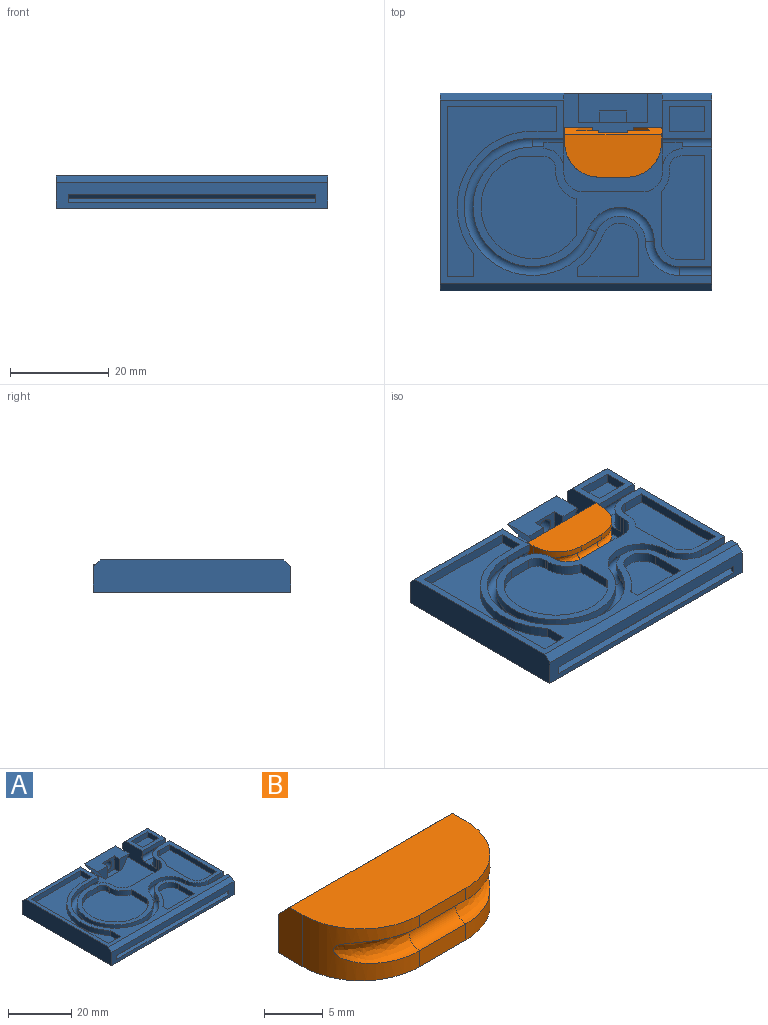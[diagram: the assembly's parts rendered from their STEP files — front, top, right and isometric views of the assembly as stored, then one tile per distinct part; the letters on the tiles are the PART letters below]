
ASSEMBLY  parts=2 mates=1
PART A: 103 faces, bbox 55x40x6.5 mm
  f0: plane 48.34x24.2mm, normal (0,0,1), area 268.4mm2, adj f6,f7,f13,f16,f17,f23,f26,f29
  f1: plane 10x7.7mm, normal (0,0,1), area 41.7mm2, adj f7,f14,f17,f52,f82,f83,f84,f85
  f2: plane 55x37.2mm, normal (0,0,1), area 312mm2, adj f6,f17,f18,f20,f21,f24,f27,f30
  f3: plane 55x5.1mm, normal (0,1,0), area 150.8mm2, adj f6,f7,f8,f9,f17,f18,f19,f34
  f4: plane 14x2.7mm, normal (0,1,0), area 27mm2, adj f8,f9,f10,f43,f56,f57
  f5: plane 55x5.1mm, normal (0,-1,0), area 200.5mm2, adj f17,f18,f19,f54,f64,f65,f66,f67
  f6: plane 16x5.6mm, normal (1,0,0), area 64.8mm2, adj f0,f2,f3,f12,f20,f34,f37,f38
  f7: plane 16x5.6mm, normal (-1,0,0), area 64.8mm2, adj f0,f1,f3,f14,f15,f34,f41,f42
  f8: plane 6x4.6mm, normal (0.82,0,-0.57), area 32.9mm2, adj f3,f4,f11,f34,f43,f55,f56
  f9: plane 6x4.6mm, normal (-0.82,0,-0.57), area 32.9mm2, adj f3,f4,f34,f43,f44,f55,f57
  f10: cylinder r=1.7mm len=3.6mm, axis (0,-1,0), area 36.5mm2, adj f4,f48,f55,f56,f57
  f11: plane 4.6x4.25mm, normal (0,-1,0), area 12.1mm2, adj f8,f34,f43,f46
  f12: cylinder r=1.25mm len=6.24mm, axis (-1,0,0), area 24.8mm2, adj f6,f13,f20,f22,f35,f36,f37
  f13: plane 2.24x1.6mm, normal (0,1,0), area 3.6mm2, adj f0,f12,f23,f36
  f14: plane 10x1.6mm, normal (0,-1,0), area 16mm2, adj f1,f7,f15,f17
  f15: cylinder r=1.25mm len=10mm, axis (-1,0,0), area 46.8mm2, adj f7,f14,f16,f17,f39,f40,f41
  f16: plane 6x1.6mm, normal (0,1,0), area 9.6mm2, adj f0,f15,f17,f40
  f17: plane 40x6.5mm, normal (1,0,0), area 243.4mm2, adj f0,f1,f2,f3,f5,f14,f15,f16
  f18: plane 40x6.5mm, normal (-1,0,0), area 258mm2, adj f2,f3,f5,f19,f53,f54
  f19: plane 55x40mm, normal (0,0,-1), area 2200mm2, adj f3,f5,f17,f18
  f20: plane 6.24x1.6mm, normal (0,-1,0), area 10mm2, adj f2,f6,f12,f21
  f21: cylinder r=13.9mm len=27.8mm, axis (0,0,1), area 96.4mm2, adj f2,f20,f22,f24
  f22: torus R=13mm, axis (0,0,1), area 329.4mm2, adj f12,f21,f23,f25
  f23: cylinder r=12.1mm len=24.2mm, axis (0,0,1), area 83.9mm2, adj f0,f13,f22,f26
  f24: cylinder r=5.1mm len=9.84mm, axis (0,0,-1), area 22.6mm2, adj f2,f21,f25,f27
  f25: torus R=6mm, axis (0,0,-1), area 96.9mm2, adj f22,f24,f26,f28
  f26: cylinder r=6.9mm len=13.31mm, axis (0,0,-1), area 30.5mm2, adj f0,f23,f25,f29
  f27: cylinder r=6.9mm len=6.9mm, axis (0,0,1), area 17.3mm2, adj f2,f24,f28,f30
  f28: torus R=6mm, axis (0,0,1), area 55.1mm2, adj f25,f27,f29,f31
  f29: cylinder r=5.1mm len=5.1mm, axis (0,0,1), area 12.8mm2, adj f0,f26,f28,f32
  f30: plane 6.58x1.6mm, normal (0,1,0), area 10.5mm2, adj f2,f17,f27,f31
  f31: cylinder r=1.25mm len=6.58mm, axis (1,0,0), area 38.4mm2, adj f17,f28,f30,f32
  f32: plane 6.58x1.6mm, normal (0,-1,0), area 10.5mm2, adj f0,f17,f29,f31
  f33: plane 12x5.6mm, normal (0,1,0), area 67.2mm2, adj f0,f34,f50,f51
  f34: plane 20x20mm, normal (0,0,1), area 347.8mm2, adj f3,f6,f7,f8,f9,f11,f33,f44
  f35: plane 1.25x1.25mm, normal (1,0,0), area 0.3mm2, adj f12,f37,f38
  f36: plane 2.47x0.35mm, normal (1,0,0), area 0.7mm2, adj f0,f12,f13,f38
  f37: plane 5.25x4mm, normal (0,0,1), area 8.4mm2, adj f6,f12,f35,f38
  f38: cylinder r=4mm len=4mm, axis (0,0,1), area 23.4mm2, adj f0,f6,f35,f36,f37
  f39: plane 1.25x1.25mm, normal (-1,0,0), area 0.3mm2, adj f15,f41,f42
  f40: plane 2.47x0.35mm, normal (-1,0,0), area 0.7mm2, adj f0,f15,f16,f42
  f41: plane 5.25x4mm, normal (0,0,1), area 8.4mm2, adj f7,f15,f39,f42
  f42: cylinder r=4mm len=4mm, axis (0,0,1), area 23.4mm2, adj f0,f7,f39,f40,f41
  f43: plane 14x6mm, normal (0,0,1), area 70.8mm2, adj f4,f8,f9,f11,f44,f46,f47,f48
  f44: plane 4.6x4.25mm, normal (0,-1,0), area 12.1mm2, adj f9,f34,f43,f47
  f45: plane 5.5x0.5mm, normal (0,1,0), area 2.8mm2, adj f34,f46,f47,f49
  f46: plane 5.1x2.4mm, normal (-1,0,0), area 12.2mm2, adj f11,f43,f45,f48,f49
  f47: plane 5.1x2.4mm, normal (1,0,0), area 12.2mm2, adj f43,f44,f45,f48,f49
  f48: plane 5.5x5.1mm, normal (0,-1,0), area 19mm2, adj f10,f43,f46,f47,f49
  f49: plane 5.5x2.4mm, normal (0,0,1), area 13.2mm2, adj f45,f46,f47,f48
  f50: cylinder r=4mm len=5.6mm, axis (0,0,-1), area 35.2mm2, adj f0,f6,f33,f34
  f51: cylinder r=4mm len=5.6mm, axis (0,0,1), area 35.2mm2, adj f0,f7,f33,f34
  f52: plane 10x1.4mm, normal (0,0.71,0.71), area 19.8mm2, adj f1,f3,f7,f17
  f53: plane 25x1.4mm, normal (0,0.71,0.71), area 49.5mm2, adj f2,f3,f6,f18
  f54: plane 55x1.4mm, normal (0,-0.71,0.71), area 108.9mm2, adj f2,f5,f17,f18
  f55: plane 9.1x0.8mm, normal (0,0.71,0.71), area 8.3mm2, adj f3,f8,f9,f10,f56,f57
  f56: plane 3.86x0.8mm, normal (0,0.71,-0.71), area 3.8mm2, adj f4,f8,f10,f55
  f57: plane 3.86x0.8mm, normal (0,0.71,-0.71), area 3.8mm2, adj f4,f9,f10,f55
  f58: plane 7.5x0.8mm, normal (0,0.71,0.71), area 8.5mm2, adj f3,f7,f59,f60
  f59: plane 7.5x0.8mm, normal (0,0.71,-0.71), area 8.5mm2, adj f3,f7,f58,f60
  f60: plane 1.6x0.8mm, normal (-1,0,0), area 0.6mm2, adj f3,f58,f59
  f61: plane 22.5x0.8mm, normal (0,0.71,-0.71), area 25.5mm2, adj f3,f6,f62,f63
  f62: plane 22.5x0.8mm, normal (0,0.71,0.71), area 25.5mm2, adj f3,f6,f61,f63
  f63: plane 1.6x0.8mm, normal (1,0,0), area 0.6mm2, adj f3,f61,f62
  f64: plane 50x0.8mm, normal (0,-0.71,0.71), area 56.6mm2, adj f5,f65,f66,f67
  f65: plane 50x0.8mm, normal (0,-0.71,-0.71), area 56.6mm2, adj f5,f64,f66,f67
  f66: plane 1.6x0.8mm, normal (-1,0,0), area 0.6mm2, adj f5,f64,f65
  f67: plane 1.6x0.8mm, normal (1,0,0), area 0.6mm2, adj f5,f64,f65
  f68: plane 22.2x2mm, normal (0,-1,0), area 44.4mm2, adj f2,f69,f74,f75
  f69: plane 34.4x2mm, normal (1,0,0), area 68.8mm2, adj f2,f68,f70,f75
  f70: plane 5.46x2mm, normal (-0.01,1,0), area 10.9mm2, adj f2,f69,f71,f75
  f71: plane 4.55x2mm, normal (-1,0,0), area 9.1mm2, adj f2,f70,f72,f75
  f72: cylinder r=15.3mm len=24.92mm, axis (0,0,1), area 68.9mm2, adj f2,f71,f73,f75
  f73: plane 4.84x2mm, normal (0,1,0), area 9.7mm2, adj f2,f72,f74,f75
  f74: plane 4.9x2mm, normal (-1,0,0), area 9.8mm2, adj f2,f68,f73,f75
  f75: plane 34.4x22.2mm, normal (0,0,1), area 245.7mm2, adj f68,f69,f70,f71,f72,f73,f74
  f76: plane 2x1.9mm, normal (1,0,0), area 3.8mm2, adj f2,f77,f80,f81
  f77: plane 12.26x2mm, normal (0,1,0), area 24.5mm2, adj f2,f76,f78,f81
  f78: plane 7.2x2mm, normal (-1,0,0), area 14.4mm2, adj f2,f77,f79,f81
  f79: cylinder r=3.7mm len=7.14mm, axis (0,0,1), area 20.5mm2, adj f2,f78,f80,f81
  f80: cylinder r=15.3mm len=6.66mm, axis (0,0,1), area 17mm2, adj f2,f76,f79,f81
  f81: plane 12.26x10.9mm, normal (0,0,1), area 96.2mm2, adj f76,f77,f78,f79,f80
  f82: plane 7.2x2mm, normal (0,-1,0), area 14.4mm2, adj f1,f83,f85,f86
  f83: plane 4.9x2mm, normal (1,0,0), area 9.8mm2, adj f1,f82,f84,f86
  f84: plane 7.2x2mm, normal (0,1,0), area 14.4mm2, adj f1,f83,f85,f86
  f85: plane 4.9x2mm, normal (-1,0,0), area 9.8mm2, adj f1,f82,f84,f86
  f86: plane 7.2x4.9mm, normal (0,0,1), area 35.3mm2, adj f82,f83,f84,f85
  f87: cylinder r=2.4mm len=2.4mm, axis (0,0,1), area 7.5mm2, adj f0,f88,f92,f93
  f88: plane 4.93x2mm, normal (0,-1,0), area 9.9mm2, adj f0,f87,f89,f93
  f89: cylinder r=10.5mm len=20.65mm, axis (0,0,1), area 81.2mm2, adj f0,f88,f90,f93
  f90: plane 7.43x2mm, normal (-1,0,0), area 14.9mm2, adj f0,f89,f91,f93
  f91: cylinder r=5.6mm len=5.4mm, axis (0,0,1), area 14.6mm2, adj f0,f90,f92,f93
  f92: plane 2x0.75mm, normal (-1,0,0), area 1.5mm2, adj f0,f87,f91,f93
  f93: plane 20.65x19.24mm, normal (0,0,1), area 310.4mm2, adj f87,f88,f89,f90,f91,f92
  f94: cylinder r=3.7mm len=3.7mm, axis (0,0,1), area 11.6mm2, adj f0,f95,f101,f102
  f95: plane 5.18x2mm, normal (0,1,0), area 10.3mm2, adj f0,f94,f96,f102
  f96: plane 21.05x2mm, normal (-1,0,0), area 42.1mm2, adj f0,f95,f97,f102
  f97: plane 4.6x2mm, normal (0,-1,0), area 9.2mm2, adj f0,f96,f98,f102
  f98: cylinder r=2.6mm len=2.6mm, axis (0,0,1), area 8.2mm2, adj f0,f97,f99,f102
  f99: plane 2x0.96mm, normal (1,0,0), area 1.9mm2, adj f0,f98,f100,f102
  f100: cylinder r=5.4mm len=3.7mm, axis (0,0,1), area 8.3mm2, adj f0,f99,f101,f102
  f101: plane 10.09x2mm, normal (1,0,0), area 20.2mm2, adj f0,f94,f100,f102
  f102: plane 21.05x8.88mm, normal (0,0,1), area 172.3mm2, adj f94,f95,f96,f97,f98,f99,f100,f101
PART B: 22 faces, bbox 19.9x10x5.4 mm
  f0: plane 5.64x4mm, normal (0,1,0), area 16.9mm2, adj f3,f6,f9,f21
  f1: plane 5.6x1.22mm, normal (0,-1,0), area 6.8mm2, adj f4,f16,f17,f18
  f2: plane 5.64x4mm, normal (0,1,0), area 16.9mm2, adj f5,f6,f15,f21
  f3: plane 5.4x3mm, normal (-1,0,0), area 15.2mm2, adj f0,f4,f6,f17,f21
  f4: plane 19.6x8.6mm, normal (0,0,1), area 147.5mm2, adj f1,f3,f5,f16,f17,f21
  f5: plane 5.4x3mm, normal (1,0,0), area 15.2mm2, adj f2,f4,f6,f16,f21
  f6: plane 19.6x10mm, normal (0,0,-1), area 123.3mm2, adj f0,f2,f3,f5,f7,f8,f9,f15
  f7: plane 5.6x1.68mm, normal (0,-1,0), area 9.4mm2, adj f6,f16,f17,f18
  f8: plane 14.77x5mm, normal (0,1,0), area 55.5mm2, adj f6,f9,f10,f11,f12,f13,f14,f15
  f9: plane 6.2x4.6mm, normal (0.82,0,0.57), area 34.6mm2, adj f0,f6,f8,f10,f21
  f10: plane 5.6x4.43mm, normal (0,0,-1), area 24.8mm2, adj f8,f9,f11,f21
  f11: plane 5.6x0.4mm, normal (1,0,0), area 2.2mm2, adj f8,f10,f12,f21
  f12: plane 5.9x5.2mm, normal (0,0,-1), area 30.7mm2, adj f8,f11,f13,f21
  f13: plane 5.6x0.4mm, normal (-1,0,0), area 2.2mm2, adj f8,f12,f14,f21
  f14: plane 5.6x4.43mm, normal (0,0,-1), area 24.8mm2, adj f8,f13,f15,f21
  f15: plane 6.2x4.6mm, normal (-0.82,0,0.57), area 34.6mm2, adj f2,f6,f8,f14,f21
  f16: cylinder r=7mm len=7mm, axis (0,0,1), area 42.2mm2, adj f1,f4,f5,f6,f7,f20
  f17: cylinder r=7mm len=7mm, axis (0,0,-1), area 42.2mm2, adj f1,f3,f4,f6,f7,f19
  f18: cylinder r=1.25mm len=5.6mm, axis (1,0,0), area 22mm2, adj f1,f7,f19,f20
  f19: bspline ~7.17x3.99mm, area 21.7mm2, adj f17,f18
  f20: bspline ~7.17x3.99mm, area 21.7mm2, adj f16,f18
  f21: plane 19.6x1.4mm, normal (0,0.71,0.71), area 23.3mm2, adj f0,f2,f3,f4,f5,f9,f10,f11
PLACE A at identity fixed
PLACE B t=(0,-7,0)mm
MATE slider A.f10 <-> B.f0  axis (0,1,0) through (7.5,20,-1.35)mm
